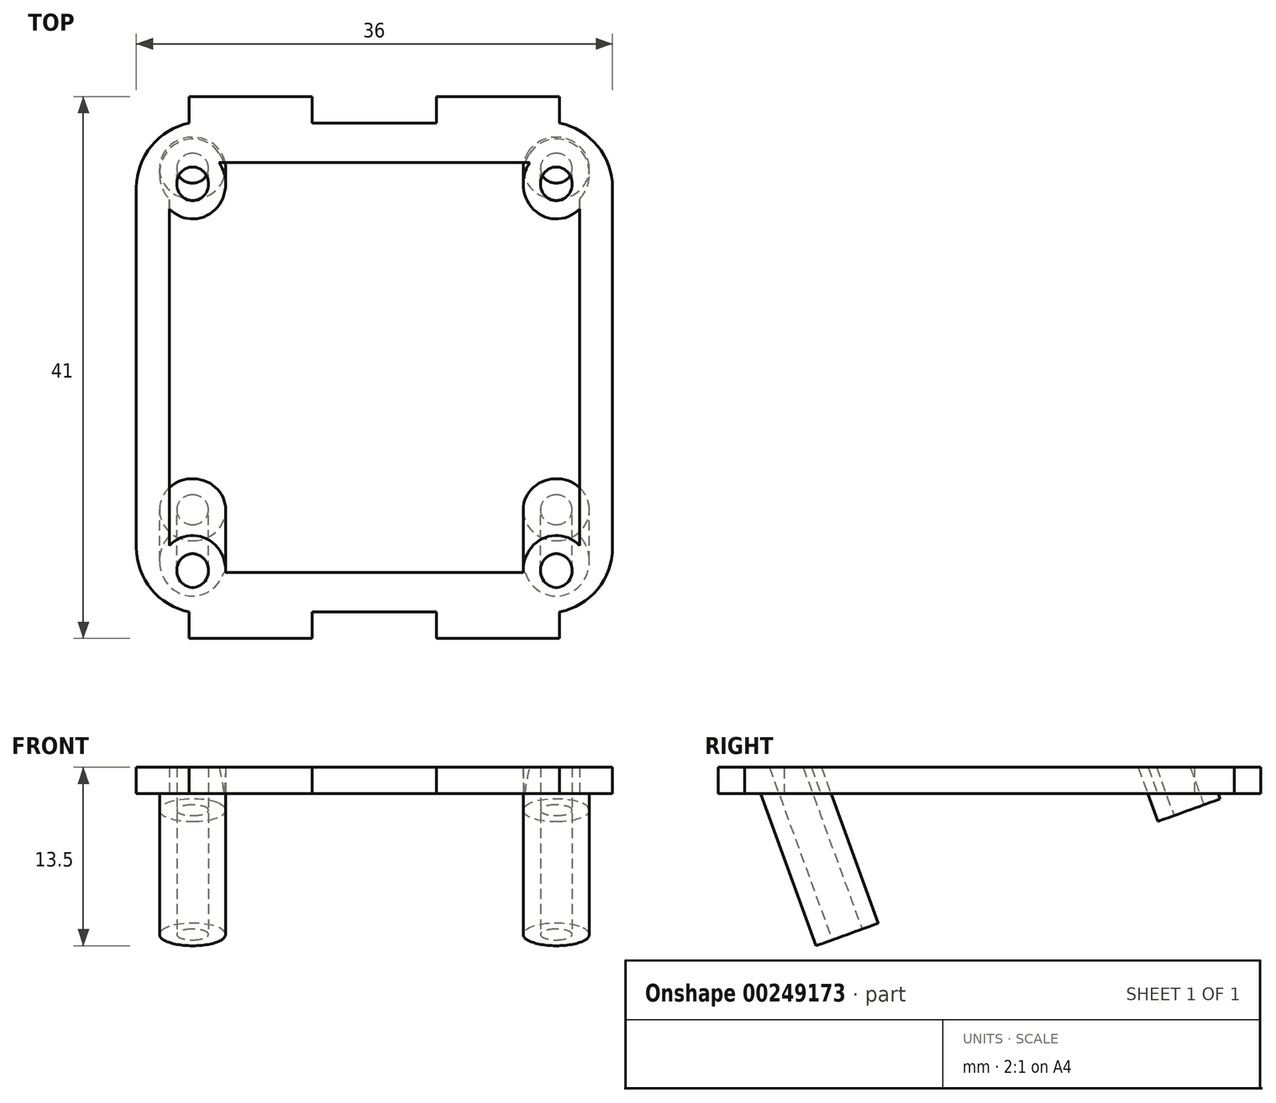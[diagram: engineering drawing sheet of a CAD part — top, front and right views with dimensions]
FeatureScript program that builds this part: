
annotation { "Feature Type Name" : "Feature", "Feature Type Description" : "" }
export const myFeature = defineFeature(function(context is Context, id is Id, definition is map)
    precondition{}
    {
        {
            var Q0;
            Q0=qCreatedBy(makeId("Top.planeOp"),FACE);
            var sketch = newSketch(context, id + "F0", { "sketchPlane" : qUnion([Q0])});
            skLineSegment(sketch, "E0", {"start": v(-18, 18.5) * mm, "end": v(-14, 18.5) * mm});
            skLineSegment(sketch, "E1", {"start": v(-14, 18.5) * mm, "end": v(-14, 20.5) * mm});
            skLineSegment(sketch, "E2", {"start": v(-14, 20.5) * mm, "end": v(-4.7, 20.5) * mm});
            skLineSegment(sketch, "E3", {"start": v(-4.7, 20.5) * mm, "end": v(-4.7, 18.5) * mm});
            skLineSegment(sketch, "E4", {"start": v(-4.7, 18.5) * mm, "end": v(4.7, 18.5) * mm});
            skLineSegment(sketch, "E5", {"start": v(4.7, 18.5) * mm, "end": v(4.7, 20.5) * mm});
            skLineSegment(sketch, "E6", {"start": v(4.7, 20.5) * mm, "end": v(14, 20.5) * mm});
            skLineSegment(sketch, "E7", {"start": v(14, 20.5) * mm, "end": v(14, 18.5) * mm});
            skLineSegment(sketch, "E8", {"start": v(14, 18.5) * mm, "end": v(18, 18.5) * mm});
            skLineSegment(sketch, "E9", {"start": v(18, 18.5) * mm, "end": v(18, -18.5) * mm});
            skLineSegment(sketch, "E10", {"start": v(18, -18.5) * mm, "end": v(14, -18.5) * mm});
            skLineSegment(sketch, "E11", {"start": v(14, -18.5) * mm, "end": v(14, -20.5) * mm});
            skLineSegment(sketch, "E12", {"start": v(14, -20.5) * mm, "end": v(4.7, -20.5) * mm});
            skLineSegment(sketch, "E13", {"start": v(4.7, -20.5) * mm, "end": v(4.7, -18.5) * mm});
            skLineSegment(sketch, "E14", {"start": v(4.7, -18.5) * mm, "end": v(-4.7, -18.5) * mm});
            skLineSegment(sketch, "E15", {"start": v(-4.7, -18.5) * mm, "end": v(-4.7, -20.5) * mm});
            skLineSegment(sketch, "E16", {"start": v(-4.7, -20.5) * mm, "end": v(-14, -20.5) * mm});
            skLineSegment(sketch, "E17", {"start": v(-14, -20.5) * mm, "end": v(-14, -18.5) * mm});
            skLineSegment(sketch, "E18", {"start": v(-14, -18.5) * mm, "end": v(-18, -18.5) * mm});
            skLineSegment(sketch, "E19", {"start": v(-18, -18.5) * mm, "end": v(-18, 18.5) * mm});
            skLineSegment(sketch, "E20", {"start": v(-55.6, 0) * mm, "end": v(55.87, 0) * mm, "construction": true});
            skLineSegment(sketch, "E21", {"start": v(0, 37.57) * mm, "end": v(0, -39.99) * mm, "construction": true});
            skLineSegment(sketch, "E22.bottom", {"start": v(-15.5, 15.5) * mm, "end": v(15.5, 15.5) * mm});
            skLineSegment(sketch, "E22.top", {"start": v(-15.5, -15.5) * mm, "end": v(15.5, -15.5) * mm});
            skLineSegment(sketch, "E22.left", {"start": v(-15.5, 15.5) * mm, "end": v(-15.5, -15.5) * mm});
            skLineSegment(sketch, "E22.right", {"start": v(15.5, 15.5) * mm, "end": v(15.5, -15.5) * mm});
            skSolve(sketch);
        }
        {
            var Q0;
            Q0 = qSketchRegion(id + "F0", true);
            extrude(context, id + "F1", {"entities" : qUnion([Q0]), "depth" : 2 * mm});
        }
        {
            var Q0;
            Q0=sQuery(id+"F0.wireOp",EDGE,"E4");
            cPlane(context, id + "F2", {"entities" : qUnion([Q0]), "cplaneType" : CPlaneType.LINE_ANGLE, "offset" : 25 * mm, "angle" : 110 * degree, "width" : 150 * mm, "height" : 150 * mm});
        }
        {
            var Q0;
            Q0=qCreatedBy(id+"F2.planeOp",FACE);
            var sketch = newSketch(context, id + "F3", { "sketchPlane" : qUnion([Q0])});
            skLineSegment(sketch, "E23.bottom", {"start": v(-13.75, -13.75) * mm, "end": v(13.75, -13.75) * mm, "construction": true});
            skLineSegment(sketch, "E23.top", {"start": v(-13.75, 13.75) * mm, "end": v(13.75, 13.75) * mm, "construction": true});
            skLineSegment(sketch, "E23.left", {"start": v(-13.75, -13.75) * mm, "end": v(-13.75, 13.75) * mm, "construction": true});
            skLineSegment(sketch, "E23.right", {"start": v(13.75, -13.75) * mm, "end": v(13.75, 13.75) * mm, "construction": true});
            skCircle(sketch, "E24", {"center": v(-13.75, -13.75) * mm, "radius": 2.5 * mm});
            skCircle(sketch, "E25", {"center": v(13.75, -13.75) * mm, "radius": 2.5 * mm});
            skCircle(sketch, "E26", {"center": v(13.75, 13.75) * mm, "radius": 2.5 * mm});
            skCircle(sketch, "E27", {"center": v(-13.75, 13.75) * mm, "radius": 2.5 * mm});
            skCircle(sketch, "E28", {"center": v(-13.75, -13.75) * mm, "radius": 1.2 * mm});
            skCircle(sketch, "E29", {"center": v(13.75, -13.75) * mm, "radius": 1.2 * mm});
            skCircle(sketch, "E30", {"center": v(13.75, 13.75) * mm, "radius": 1.2 * mm});
            skCircle(sketch, "E31", {"center": v(-13.75, 13.75) * mm, "radius": 1.2 * mm});
            skSolve(sketch);
        }
        {
            var Q0;
            Q0 = qSketchRegion(id + "F3", true);
            var Q1;
            Q1=makeQuery(id+"F1.opExtrude","CAP_FACE",FACE,{"disambiguationData":[OSD([sQuery(id+"F0.wireOp",EDGE,"E0"),sQuery(id+"F0.wireOp",EDGE,"E1"),sQuery(id+"F0.wireOp",EDGE,"E2"),sQuery(id+"F0.wireOp",EDGE,"E3"),sQuery(id+"F0.wireOp",EDGE,"E4"),sQuery(id+"F0.wireOp",EDGE,"E5"),sQuery(id+"F0.wireOp",EDGE,"E6"),sQuery(id+"F0.wireOp",EDGE,"E7"),sQuery(id+"F0.wireOp",EDGE,"E8"),sQuery(id+"F0.wireOp",EDGE,"E9"),sQuery(id+"F0.wireOp",EDGE,"E10"),sQuery(id+"F0.wireOp",EDGE,"E11"),sQuery(id+"F0.wireOp",EDGE,"E12"),sQuery(id+"F0.wireOp",EDGE,"E13"),sQuery(id+"F0.wireOp",EDGE,"E14"),sQuery(id+"F0.wireOp",EDGE,"E15"),sQuery(id+"F0.wireOp",EDGE,"E16"),sQuery(id+"F0.wireOp",EDGE,"E17"),sQuery(id+"F0.wireOp",EDGE,"E18"),sQuery(id+"F0.wireOp",EDGE,"E19"),sQuery(id+"F0.wireOp",EDGE,"E22.bottom"),sQuery(id+"F0.wireOp",EDGE,"E22.top"),sQuery(id+"F0.wireOp",EDGE,"E22.left"),sQuery(id+"F0.wireOp",EDGE,"E22.right")])],"isStart":false});
            var Q2;
            Q2=makeQuery(id+"F1.opExtrude","SWEPT_BODY",BODY,{"disambiguationData":[OSD([sQuery(id+"F0.wireOp",EDGE,"E0"),sQuery(id+"F0.wireOp",EDGE,"E1"),sQuery(id+"F0.wireOp",EDGE,"E2"),sQuery(id+"F0.wireOp",EDGE,"E3"),sQuery(id+"F0.wireOp",EDGE,"E4"),sQuery(id+"F0.wireOp",EDGE,"E5"),sQuery(id+"F0.wireOp",EDGE,"E6"),sQuery(id+"F0.wireOp",EDGE,"E7"),sQuery(id+"F0.wireOp",EDGE,"E8"),sQuery(id+"F0.wireOp",EDGE,"E9"),sQuery(id+"F0.wireOp",EDGE,"E10"),sQuery(id+"F0.wireOp",EDGE,"E11"),sQuery(id+"F0.wireOp",EDGE,"E12"),sQuery(id+"F0.wireOp",EDGE,"E13"),sQuery(id+"F0.wireOp",EDGE,"E14"),sQuery(id+"F0.wireOp",EDGE,"E15"),sQuery(id+"F0.wireOp",EDGE,"E16"),sQuery(id+"F0.wireOp",EDGE,"E17"),sQuery(id+"F0.wireOp",EDGE,"E18"),sQuery(id+"F0.wireOp",EDGE,"E19"),sQuery(id+"F0.wireOp",EDGE,"E22.bottom"),sQuery(id+"F0.wireOp",EDGE,"E22.top"),sQuery(id+"F0.wireOp",EDGE,"E22.left"),sQuery(id+"F0.wireOp",EDGE,"E22.right")])]});
            extrude(context, id + "F4", {"entities" : qUnion([Q0]), "operationType" : NewBodyOperationType.ADD, "endBound" : BoundingType.UP_TO_SURFACE, "endBoundEntityFace" : qUnion([Q1]), "endBoundEntityBody" : qUnion([Q2]), "depth" : 25 * mm});
        }
        {
            var Q0;
            Q0=makeQuery(id+"F3.imprint","IMPRINT",FACE,{"disambiguationData":[TD([[makeQuery(id+"F3.imprint","IMPRINT",EDGE,{"derivedFrom":sQuery(id+"F3.wireOp",EDGE,"E28")}),1.0]])]});
            var Q1;
            Q1=makeQuery(id+"F3.imprint","IMPRINT",FACE,{"disambiguationData":[TD([[makeQuery(id+"F3.imprint","IMPRINT",EDGE,{"derivedFrom":sQuery(id+"F3.wireOp",EDGE,"E29")}),1.0]])]});
            var Q2;
            Q2=makeQuery(id+"F3.imprint","IMPRINT",FACE,{"disambiguationData":[TD([[makeQuery(id+"F3.imprint","IMPRINT",EDGE,{"derivedFrom":sQuery(id+"F3.wireOp",EDGE,"E31")}),1.0]])]});
            var Q3;
            Q3=makeQuery(id+"F3.imprint","IMPRINT",FACE,{"disambiguationData":[TD([[makeQuery(id+"F3.imprint","IMPRINT",EDGE,{"derivedFrom":sQuery(id+"F3.wireOp",EDGE,"E30")}),1.0]])]});
            var Q4;
            Q4=sQuery(id+"F3.wireOp",EDGE,"E28");
            var Q5;
            Q5=sQuery(id+"F3.wireOp",EDGE,"E29");
            var Q6;
            Q6=sQuery(id+"F3.wireOp",EDGE,"E30");
            var Q7;
            Q7=sQuery(id+"F3.wireOp",EDGE,"E31");
            extrude(context, id + "F5", {"entities" : qUnion([Q0, Q1, Q2, Q3]), "operationType" : NewBodyOperationType.REMOVE, "surfaceEntities" : qUnion([Q4, Q5, Q6, Q7]), "endBound" : BoundingType.THROUGH_ALL, "depth" : 25 * mm});
        }
        {
            var Q0;
            Q0=makeQuery(id+"F1.opExtrude","SWEPT_EDGE",EDGE,{"disambiguationData":[OSD([sQuery(id+"F0.wireOp",EDGE,"E9"),sQuery(id+"F0.wireOp",EDGE,"E10")])]});
            var Q1;
            Q1=makeQuery(id+"F1.opExtrude","SWEPT_EDGE",EDGE,{"disambiguationData":[OSD([sQuery(id+"F0.wireOp",EDGE,"E18"),sQuery(id+"F0.wireOp",EDGE,"E19")])]});
            var Q2;
            Q2=makeQuery(id+"F1.opExtrude","SWEPT_EDGE",EDGE,{"disambiguationData":[OSD([sQuery(id+"F0.wireOp",EDGE,"E0"),sQuery(id+"F0.wireOp",EDGE,"E19")])]});
            var Q3;
            Q3=makeQuery(id+"F1.opExtrude","SWEPT_EDGE",EDGE,{"disambiguationData":[OSD([sQuery(id+"F0.wireOp",EDGE,"E8"),sQuery(id+"F0.wireOp",EDGE,"E9")])]});
            fillet(context, id + "F6", {"entities" : qUnion([Q0, Q1, Q2, Q3]), "radius" : 5 * mm, "tangentPropagation" : true, "allowEdgeOverflow" : false});
        }
    });
